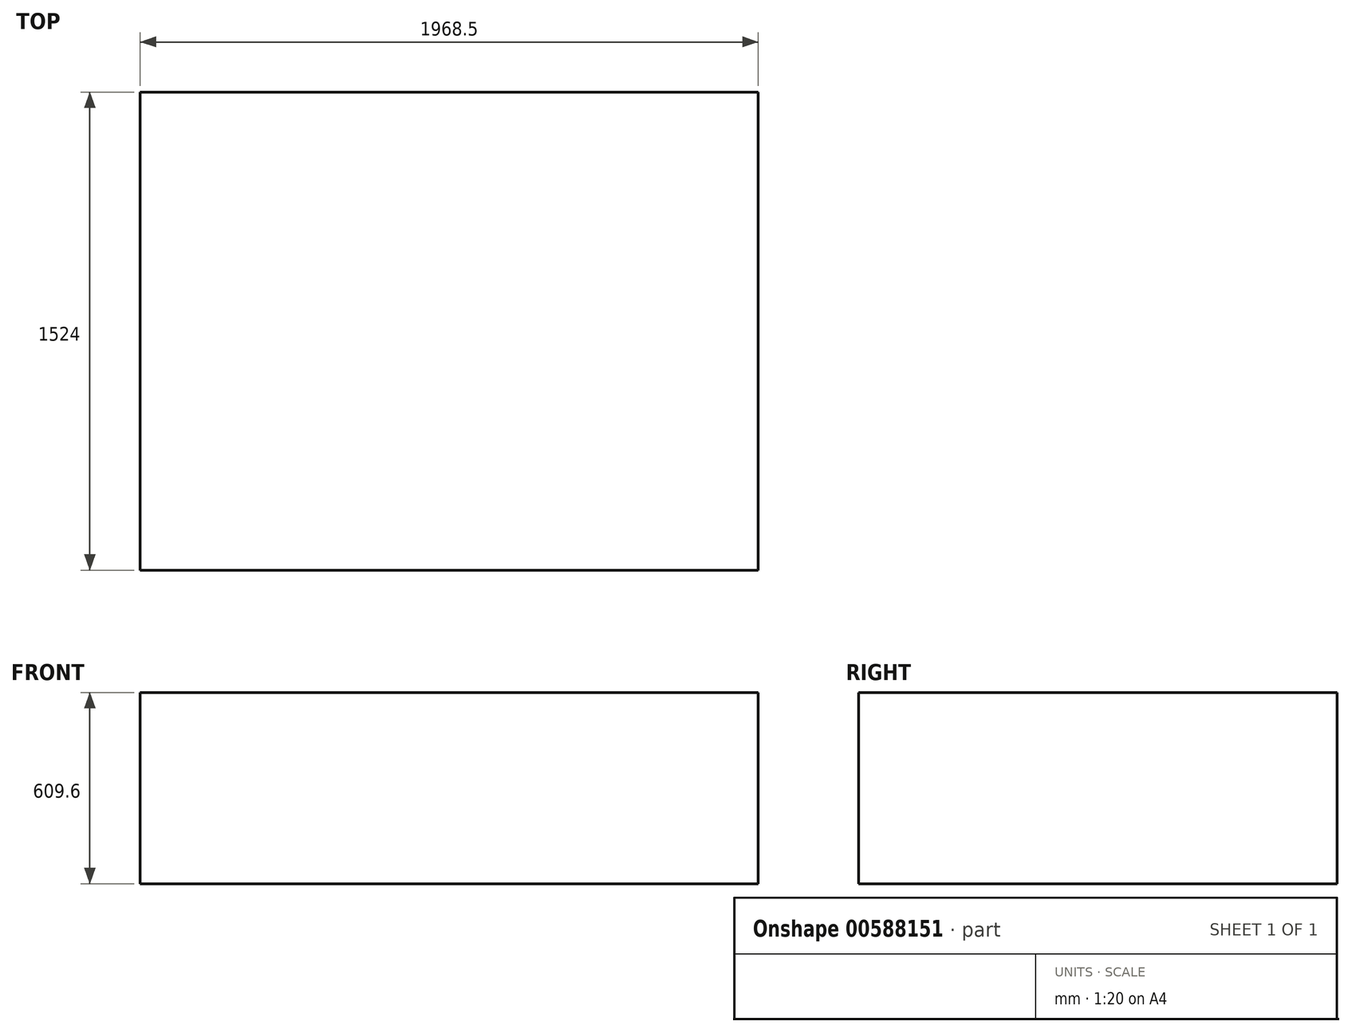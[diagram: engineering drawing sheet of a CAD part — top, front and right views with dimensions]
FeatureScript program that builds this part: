
annotation { "Feature Type Name" : "Feature", "Feature Type Description" : "" }
export const myFeature = defineFeature(function(context is Context, id is Id, definition is map)
    precondition{}
    {
        {
            var Q0;
            Q0=qCreatedBy(makeId("Top.planeOp"),FACE);
            var sketch = newSketch(context, id + "F0", { "sketchPlane" : qUnion([Q0])});
            skLineSegment(sketch, "E0.bottom", {"start": v(984.25, 762) * mm, "end": v(-984.25, 762) * mm});
            skLineSegment(sketch, "E0.top", {"start": v(984.25, -762) * mm, "end": v(-984.25, -762) * mm});
            skLineSegment(sketch, "E0.left", {"start": v(984.25, 762) * mm, "end": v(984.25, -762) * mm});
            skLineSegment(sketch, "E0.right", {"start": v(-984.25, 762) * mm, "end": v(-984.25, -762) * mm});
            skPoint(sketch, "E0.middle", {"position": v(0, 0) * mm});
            skSolve(sketch);
        }
        {
            var Q0;
            Q0=makeQuery(id+"F0.imprint","IMPRINT",FACE,{"disambiguationData":[TD([[makeQuery(id+"F0.imprint","IMPRINT",EDGE,{"derivedFrom":sQuery(id+"F0.wireOp",EDGE,"E0.bottom")}),1.0]])]});
            extrude(context, id + "F1", {"entities" : qUnion([Q0]), "depth" : 609.6 * mm, "offsetDistance" : 25.4 * mm});
        }
    });
